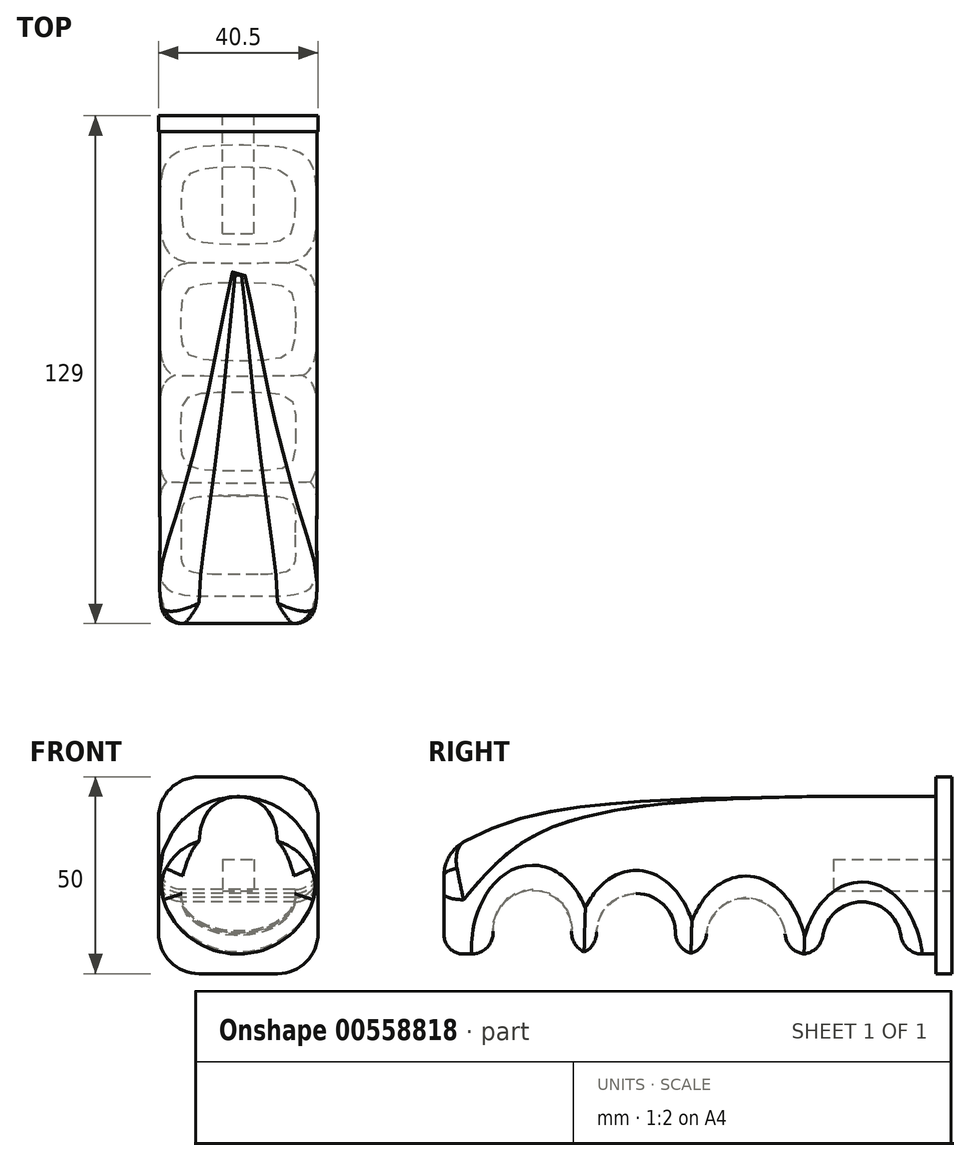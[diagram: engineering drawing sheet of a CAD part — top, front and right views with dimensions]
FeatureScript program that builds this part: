
annotation { "Feature Type Name" : "Feature", "Feature Type Description" : "" }
export const myFeature = defineFeature(function(context is Context, id is Id, definition is map)
    precondition{}
    {
        {
            var Q0;
            Q0=qCreatedBy(makeId("Front.planeOp"),FACE);
            var sketch = newSketch(context, id + "F0", { "sketchPlane" : qUnion([Q0])});
            skCircle(sketch, "E0", {"center": v(0, 0) * mm, "radius": 20 * mm});
            skSolve(sketch);
        }
        {
            var Q0;
            Q0=makeQuery(id+"F0.imprint","IMPRINT",FACE,{"disambiguationData":[TD([[makeQuery(id+"F0.imprint","IMPRINT",EDGE,{"derivedFrom":sQuery(id+"F0.wireOp",EDGE,"E0")}),1.0]])]});
            extrude(context, id + "F1", {"entities" : qUnion([Q0]), "depth" : 125 * mm, "offsetDistance" : 25 * mm});
        }
        {
            var Q0;
            Q0=qCreatedBy(makeId("Right.planeOp"),FACE);
            var sketch = newSketch(context, id + "F2", { "sketchPlane" : qUnion([Q0])});
            skCircle(sketch, "E1", {"center": v(-18.85, -16.72) * mm, "radius": 10 * mm});
            skCircle(sketch, "E2.1.0.0", {"center": v(-48.3, -15.63) * mm, "radius": 10 * mm});
            skCircle(sketch, "E2.2.0.0", {"center": v(-76.23, -14.6) * mm, "radius": 10 * mm});
            skCircle(sketch, "E2.3.0.0", {"center": v(-102.54, -13.62) * mm, "radius": 10 * mm});
            skPoint(sketch, "E3.left.start.orphan", {"position": v(0, 17.47) * mm});
            skLineSegment(sketch, "E4", {"start": v(0, -17.42) * mm, "end": v(-125.2, -12.78) * mm});
            skSolve(sketch);
        }
        {
            var Q0;
            Q0=makeQuery(id+"F2.imprint","IMPRINT",FACE,{"disambiguationData":[TD([[makeQuery(id+"F2.imprint","IMPRINT",EDGE,{"derivedFrom":sQuery(id+"F2.wireOp",EDGE,"E2.1.0.0")}),1.0]])]});
            var Q1;
            Q1=makeQuery(id+"F2.imprint","IMPRINT",FACE,{"disambiguationData":[TD([[makeQuery(id+"F2.imprint","IMPRINT",EDGE,{"derivedFrom":sQuery(id+"F2.wireOp",EDGE,"E1")}),1.0]])]});
            var Q2;
            Q2=makeQuery(id+"F2.imprint","IMPRINT",FACE,{"disambiguationData":[TD([[makeQuery(id+"F2.imprint","IMPRINT",EDGE,{"derivedFrom":sQuery(id+"F2.wireOp",EDGE,"E2.2.0.0")}),1.0]])]});
            var Q3;
            Q3=makeQuery(id+"F2.imprint","IMPRINT",FACE,{"disambiguationData":[TD([[makeQuery(id+"F2.imprint","IMPRINT",EDGE,{"derivedFrom":sQuery(id+"F2.wireOp",EDGE,"E2.3.0.0")}),1.0]])]});
            extrude(context, id + "F3", {"entities" : qUnion([Q0, Q1, Q2, Q3]), "operationType" : NewBodyOperationType.REMOVE, "endBound" : BoundingType.SYMMETRIC, "depth" : 60.4 * mm, "offsetDistance" : 25 * mm});
        }
        {
            var Q0;
            Q0=makeQuery(id+"F1.opExtrude","CAP_FACE",FACE,{"disambiguationData":[OSD([sQuery(id+"F0.wireOp",EDGE,"E0")])],"isStart":true});
            var sketch = newSketch(context, id + "F4", { "sketchPlane" : qUnion([Q0])});
            skLineSegment(sketch, "E5.bottom", {"start": v(-10, 25) * mm, "end": v(10, 25) * mm});
            skLineSegment(sketch, "E5.top", {"start": v(-10, -25) * mm, "end": v(10, -25) * mm});
            skLineSegment(sketch, "E5.left", {"start": v(-20.25, 14.75) * mm, "end": v(-20.25, -14.75) * mm});
            skLineSegment(sketch, "E5.right", {"start": v(20.25, 14.75) * mm, "end": v(20.25, -14.75) * mm});
            skPoint(sketch, "E5.middle", {"position": v(0, 0) * mm});
            skPoint(sketch, "E6.visualSharp", {"position": v(-20.25, 25) * mm});
            skArc(sketch, "E6.filletArc", {"start": v(-10, 25) * mm, "mid": v(-17.25, 22) * mm, "end": v(-20.25, 14.75) * mm});
            skArc(sketch, "E7.MirrorCS", {"start": v(-10, -25) * mm, "mid": v(-17.25, -22) * mm, "end": v(-20.25, -14.75) * mm});
            skArc(sketch, "E8.MirrorCS", {"start": v(10, 25) * mm, "mid": v(17.25, 22) * mm, "end": v(20.25, 14.75) * mm});
            skArc(sketch, "E9.MirrorCS", {"start": v(10, -25) * mm, "mid": v(17.25, -22) * mm, "end": v(20.25, -14.75) * mm});
            skPoint(sketch, "E10.orphan", {"position": v(20.25, 25) * mm});
            skPoint(sketch, "E11.orphan", {"position": v(20.25, -25) * mm});
            skPoint(sketch, "E12.orphan", {"position": v(-20.25, -25) * mm});
            skSolve(sketch);
        }
        {
            var Q0;
            Q0=makeQuery(id+"F4.imprint","IMPRINT",FACE,{"disambiguationData":[TD([[makeQuery(id+"F4.imprint","IMPRINT",EDGE,{"derivedFrom":sQuery(id+"F4.wireOp",EDGE,"E5.bottom")}),-1.0]])]});
            var Q1;
            Q1=makeQuery(id+"F4.imprint","IMPRINT",FACE,{"disambiguationData":[TD([[makeQuery(id+"F4.imprint","IMPRINT",EDGE,{"derivedFrom":makeQuery(id+"F1.opExtrude","CAP_EDGE",EDGE,{"disambiguationData":[OSD([sQuery(id+"F0.wireOp",EDGE,"E0")])],"isStart":true})}),-1.0]])]});
            extrude(context, id + "F5", {"entities" : qUnion([Q0, Q1]), "operationType" : NewBodyOperationType.ADD, "depth" : 4 * mm, "offsetDistance" : 25 * mm});
        }
        {
            var Q0;
            Q0=makeQuery(id+"F5.opExtrude","CAP_FACE",FACE,{"disambiguationData":[OSD([sQuery(id+"F4.wireOp",EDGE,"E5.bottom"),sQuery(id+"F4.wireOp",EDGE,"E5.top"),sQuery(id+"F4.wireOp",EDGE,"E5.left"),sQuery(id+"F4.wireOp",EDGE,"E5.right"),sQuery(id+"F4.wireOp",EDGE,"E6.filletArc"),sQuery(id+"F4.wireOp",EDGE,"E7.MirrorCS"),sQuery(id+"F4.wireOp",EDGE,"E8.MirrorCS"),sQuery(id+"F4.wireOp",EDGE,"E9.MirrorCS")])],"isStart":false});
            var sketch = newSketch(context, id + "F6", { "sketchPlane" : qUnion([Q0])});
            skLineSegment(sketch, "E13.bottom", {"start": v(4, 4) * mm, "end": v(-4, 4) * mm});
            skLineSegment(sketch, "E13.top", {"start": v(4, -4) * mm, "end": v(-4, -4) * mm});
            skLineSegment(sketch, "E13.left", {"start": v(4, 4) * mm, "end": v(4, -4) * mm});
            skLineSegment(sketch, "E13.right", {"start": v(-4, 4) * mm, "end": v(-4, -4) * mm});
            skPoint(sketch, "E13.middle", {"position": v(0, 0) * mm});
            skSolve(sketch);
        }
        {
            var Q0;
            Q0=makeQuery(id+"F6.imprint","IMPRINT",FACE,{"disambiguationData":[TD([[makeQuery(id+"F6.imprint","IMPRINT",EDGE,{"derivedFrom":sQuery(id+"F6.wireOp",EDGE,"E13.bottom")}),1.0]])]});
            extrude(context, id + "F7", {"entities" : qUnion([Q0]), "operationType" : NewBodyOperationType.REMOVE, "oppositeDirection" : true, "depth" : 30 * mm, "offsetDistance" : 25 * mm});
        }
        {
            var Q0;
            Q0=makeQuery(id+"F3.boolean.opBoolean","COPY",FACE,{"derivedFrom":makeQuery(id+"F3.opExtrude","SWEPT_FACE",FACE,{"disambiguationData":[OSD([sQuery(id+"F2.wireOp",EDGE,"E2.3.0.0")])]})});
            var Q1;
            Q1=makeQuery(id+"F3.boolean.opBoolean","COPY",FACE,{"derivedFrom":makeQuery(id+"F3.opExtrude","SWEPT_FACE",FACE,{"disambiguationData":[OSD([sQuery(id+"F2.wireOp",EDGE,"E2.2.0.0")])]})});
            var Q2;
            Q2=makeQuery(id+"F3.boolean.opBoolean","COPY",FACE,{"derivedFrom":makeQuery(id+"F3.opExtrude","SWEPT_FACE",FACE,{"disambiguationData":[OSD([sQuery(id+"F2.wireOp",EDGE,"E2.1.0.0")])]})});
            var Q3;
            Q3=makeQuery(id+"F3.boolean.opBoolean","COPY",FACE,{"derivedFrom":makeQuery(id+"F3.opExtrude","SWEPT_FACE",FACE,{"disambiguationData":[OSD([sQuery(id+"F2.wireOp",EDGE,"E1")])]})});
            fillet(context, id + "F8", {"entities" : qUnion([Q0, Q1, Q2, Q3]), "radius" : 5.5 * mm, "tangentPropagation" : true, "allowEdgeOverflow" : false});
        }
        {
            var Q0;
            Q0=makeQuery(id+"F1.opExtrude","CAP_FACE",FACE,{"disambiguationData":[OSD([sQuery(id+"F0.wireOp",EDGE,"E0")])],"isStart":false});
            fillet(context, id + "F9", {"entities" : qUnion([Q0]), "radius" : 5 * mm, "tangentPropagation" : true, "allowEdgeOverflow" : false});
        }
        {
            var Q0;
            Q0=qCreatedBy(makeId("Right.planeOp"),FACE);
            var sketch = newSketch(context, id + "F10", { "sketchPlane" : qUnion([Q0])});
            skFitSpline(sketch, "E14", {"points": [v(0, 20.23) * mm, v(-98.41, 16.12) * mm, v(-133.5, 0) * mm], "startDerivative": vector(-178.39, -1.77) * mm, "endDerivative": vector(-101.6, -68.92) * mm});
            skLineSegment(sketch, "E15", {"start": v(-133.5, 0) * mm, "end": v(-135.09, 27.7) * mm});
            skLineSegment(sketch, "E16", {"start": v(-135.09, 27.7) * mm, "end": v(0, 20.23) * mm});
            skSolve(sketch);
        }
        {
            var Q0;
            Q0=makeQuery(id+"F10.imprint","IMPRINT",FACE,{"disambiguationData":[TD([[makeQuery(id+"F10.imprint","IMPRINT",EDGE,{"derivedFrom":sQuery(id+"F10.wireOp",EDGE,"E14")}),-1.0]])]});
            extrude(context, id + "F11", {"entities" : qUnion([Q0]), "operationType" : NewBodyOperationType.REMOVE, "endBound" : BoundingType.SYMMETRIC, "depth" : 52.8 * mm, "offsetDistance" : 25 * mm});
        }
        {
            var Q0;
            Q0=makeQuery(id+"F11.boolean.opBoolean","COPY",FACE,{"derivedFrom":makeQuery(id+"F11.opExtrude","SWEPT_FACE",FACE,{"disambiguationData":[OSD([sQuery(id+"F10.wireOp",EDGE,"E14")])]})});
            fillet(context, id + "F12", {"entities" : qUnion([Q0]), "radius" : 10 * mm, "tangentPropagation" : true, "allowEdgeOverflow" : false});
        }
    });
